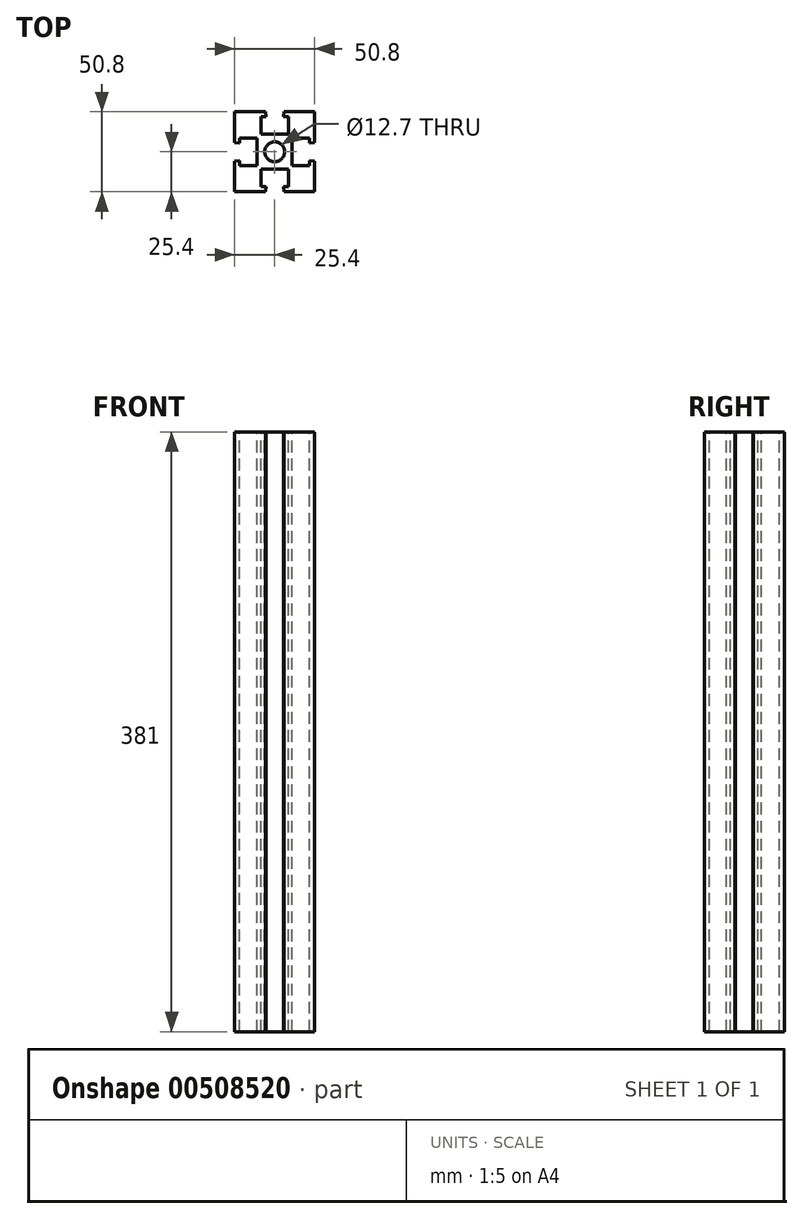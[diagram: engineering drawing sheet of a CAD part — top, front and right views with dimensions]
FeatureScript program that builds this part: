
annotation { "Feature Type Name" : "Feature", "Feature Type Description" : "" }
export const myFeature = defineFeature(function(context is Context, id is Id, definition is map)
    precondition{}
    {
        {
            var Q0;
            Q0=qCreatedBy(makeId("Top.planeOp"),FACE);
            var sketch = newSketch(context, id + "F0", { "sketchPlane" : qUnion([Q0])});
            skLineSegment(sketch, "E0.bottom", {"start": v(0, 0) * mm, "end": v(50.8, 0) * mm});
            skLineSegment(sketch, "E0.top", {"start": v(0, -50.8) * mm, "end": v(50.8, -50.8) * mm});
            skLineSegment(sketch, "E0.left", {"start": v(0, 0) * mm, "end": v(0, -50.8) * mm});
            skLineSegment(sketch, "E0.right", {"start": v(50.8, 0) * mm, "end": v(50.8, -50.8) * mm});
            skSolve(sketch);
        }
        {
            var Q0;
            Q0=qSketchRegion(id+"F0",true);
            extrude(context, id + "F1", {"entities" : qUnion([Q0]), "depth" : 381 * mm, "offsetDistance" : 25.4 * mm});
        }
        {
            var Q0;
            Q0=makeQuery(id+"F1.opExtrude","CAP_FACE",FACE,{"disambiguationData":[OSD([sQuery(id+"F0.wireOp",EDGE,"E0.bottom"),sQuery(id+"F0.wireOp",EDGE,"E0.top"),sQuery(id+"F0.wireOp",EDGE,"E0.left"),sQuery(id+"F0.wireOp",EDGE,"E0.right")])],"isStart":false});
            var sketch = newSketch(context, id + "F2", { "sketchPlane" : qUnion([Q0])});
            skLineSegment(sketch, "E1", {"start": v(25.4, 0) * mm, "end": v(25.4, -50.8) * mm, "construction": true});
            skLineSegment(sketch, "E2", {"start": v(0, -25.4) * mm, "end": v(50.8, -25.4) * mm, "construction": true});
            skCircle(sketch, "E3", {"center": v(25.4, -25.4) * mm, "radius": 6.35 * mm});
            skLineSegment(sketch, "E4", {"start": v(16.67, -3.18) * mm, "end": v(19.84, -3.18) * mm});
            skLineSegment(sketch, "E5", {"start": v(47.63, -16.67) * mm, "end": v(47.63, -19.84) * mm});
            skLineSegment(sketch, "E6", {"start": v(16.67, -47.63) * mm, "end": v(19.84, -47.63) * mm});
            skLineSegment(sketch, "E7", {"start": v(3.18, -16.67) * mm, "end": v(3.18, -19.84) * mm});
            skLineSegment(sketch, "E8", {"start": v(14.29, -16.67) * mm, "end": v(14.29, -34.13) * mm});
            skLineSegment(sketch, "E9", {"start": v(16.67, -14.29) * mm, "end": v(34.13, -14.29) * mm});
            skLineSegment(sketch, "E10", {"start": v(36.51, -16.67) * mm, "end": v(36.51, -34.13) * mm});
            skLineSegment(sketch, "E11", {"start": v(16.67, -36.51) * mm, "end": v(34.13, -36.51) * mm});
            skLineSegment(sketch, "E12", {"start": v(3.18, -34.13) * mm, "end": v(14.29, -34.13) * mm});
            skLineSegment(sketch, "E13", {"start": v(3.18, -16.67) * mm, "end": v(14.29, -16.67) * mm});
            skLineSegment(sketch, "E14", {"start": v(16.67, -3.18) * mm, "end": v(16.67, -14.29) * mm});
            skLineSegment(sketch, "E15", {"start": v(34.13, -3.17) * mm, "end": v(34.13, -14.29) * mm});
            skLineSegment(sketch, "E16", {"start": v(47.63, -16.67) * mm, "end": v(36.51, -16.67) * mm});
            skLineSegment(sketch, "E17", {"start": v(47.63, -34.13) * mm, "end": v(36.51, -34.13) * mm});
            skLineSegment(sketch, "E18", {"start": v(34.13, -47.63) * mm, "end": v(34.13, -36.51) * mm});
            skLineSegment(sketch, "E19", {"start": v(16.67, -47.63) * mm, "end": v(16.67, -36.51) * mm});
            skLineSegment(sketch, "E20", {"start": v(0, -19.59) * mm, "end": v(3.18, -19.84) * mm});
            skLineSegment(sketch, "E21", {"start": v(3.18, -30.96) * mm, "end": v(0, -31.21) * mm});
            skLineSegment(sketch, "E22", {"start": v(19.84, -47.63) * mm, "end": v(19.59, -50.8) * mm});
            skLineSegment(sketch, "E23", {"start": v(30.96, -47.63) * mm, "end": v(31.21, -50.8) * mm});
            skLineSegment(sketch, "E24", {"start": v(47.63, -30.96) * mm, "end": v(50.8, -31.21) * mm});
            skLineSegment(sketch, "E25", {"start": v(47.63, -19.84) * mm, "end": v(50.8, -19.59) * mm});
            skLineSegment(sketch, "E26", {"start": v(30.96, -3.18) * mm, "end": v(31.21, 0) * mm});
            skLineSegment(sketch, "E27", {"start": v(19.84, -3.18) * mm, "end": v(19.59, 0) * mm});
            skPoint(sketch, "E28", {"position": v(25.4, -3.18) * mm});
            skPoint(sketch, "E29", {"position": v(47.63, -25.4) * mm});
            skPoint(sketch, "E30", {"position": v(25.4, -47.63) * mm});
            skPoint(sketch, "E31", {"position": v(3.18, -25.4) * mm});
            skLineSegment(sketch, "E32.trimOffspring", {"start": v(3.18, -30.96) * mm, "end": v(3.18, -34.13) * mm});
            skLineSegment(sketch, "E33.trimOffspring", {"start": v(30.96, -47.63) * mm, "end": v(34.13, -47.63) * mm});
            skLineSegment(sketch, "E34.trimOffspring", {"start": v(47.63, -30.96) * mm, "end": v(47.63, -34.13) * mm});
            skLineSegment(sketch, "E35.trimOffspring", {"start": v(30.96, -3.17) * mm, "end": v(34.13, -3.17) * mm});
            skSolve(sketch);
        }
        {
            var Q0;
            Q0=qSketchRegion(id+"F2",true);
            var Q1;
            Q1=makeQuery(id+"F2.imprint","IMPRINT",FACE,{"disambiguationData":[TD([[makeQuery(id+"F2.imprint","IMPRINT",EDGE,{"derivedFrom":sQuery(id+"F2.wireOp",EDGE,"E6")}),1.0]])]});
            var Q2;
            Q2=makeQuery(id+"F2.imprint","IMPRINT",FACE,{"disambiguationData":[TD([[makeQuery(id+"F2.imprint","IMPRINT",EDGE,{"derivedFrom":sQuery(id+"F2.wireOp",EDGE,"E5")}),-1.0]])]});
            var Q3;
            Q3=makeQuery(id+"F2.imprint","IMPRINT",FACE,{"disambiguationData":[TD([[makeQuery(id+"F2.imprint","IMPRINT",EDGE,{"derivedFrom":sQuery(id+"F2.wireOp",EDGE,"E7")}),1.0]])]});
            var Q4;
            Q4=makeQuery(id+"F2.imprint","IMPRINT",FACE,{"disambiguationData":[TD([[makeQuery(id+"F2.imprint","IMPRINT",EDGE,{"derivedFrom":sQuery(id+"F2.wireOp",EDGE,"E4")}),-1.0]])]});
            extrude(context, id + "F3", {"entities" : qUnion([Q0, Q1, Q2, Q3, Q4]), "operationType" : NewBodyOperationType.REMOVE, "oppositeDirection" : true, "depth" : 508 * mm, "offsetDistance" : 25.4 * mm});
        }
    });
